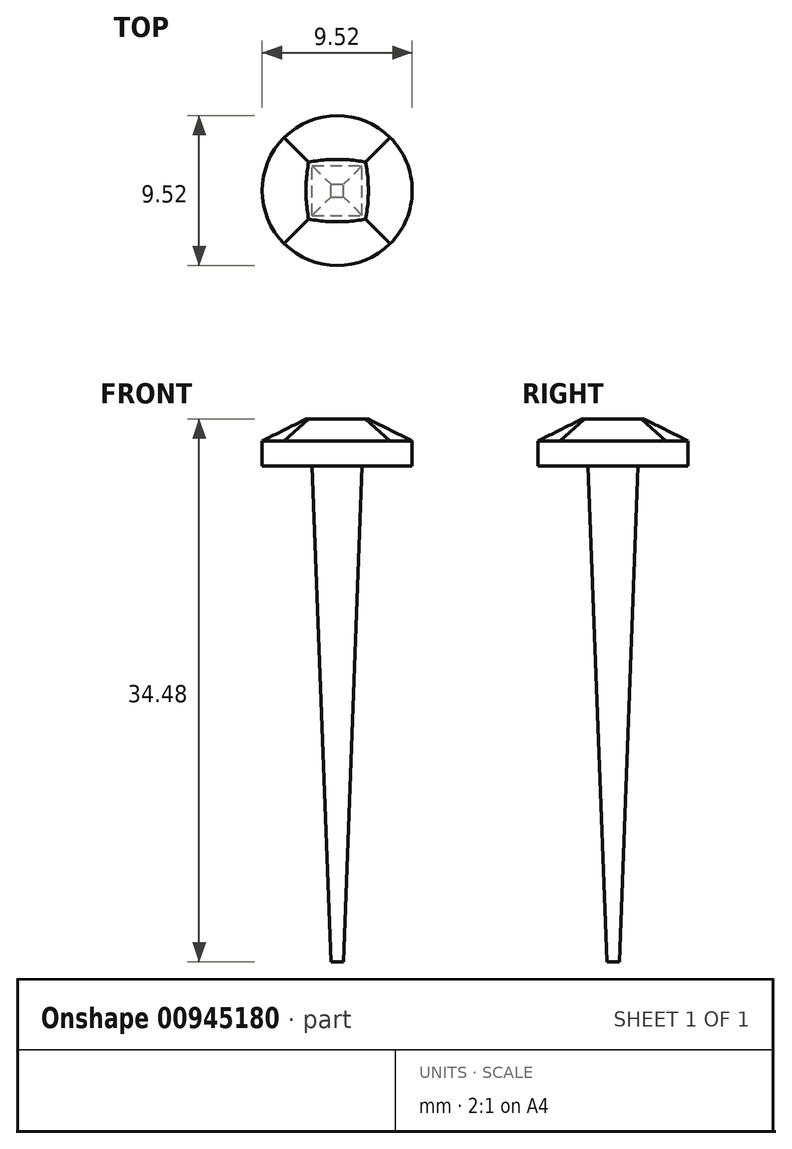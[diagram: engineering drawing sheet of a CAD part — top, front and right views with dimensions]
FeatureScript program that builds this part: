
annotation { "Feature Type Name" : "Feature", "Feature Type Description" : "" }
export const myFeature = defineFeature(function(context is Context, id is Id, definition is map)
    precondition{}
    {
        {
            var Q0;
            Q0=qCreatedBy(makeId("Top.planeOp"),FACE);
            var sketch = newSketch(context, id + "F0", { "sketchPlane" : qUnion([Q0])});
            skCircle(sketch, "E0", {"center": v(0, 0) * mm, "radius": 4.76 * mm});
            skSolve(sketch);
        }
        {
            var Q0;
            Q0=qCreatedBy(makeId("Top.planeOp"),FACE);
            cPlane(context, id + "F1", {"entities" : qUnion([Q0]), "cplaneType" : CPlaneType.OFFSET, "offset" : 1.59 * mm, "width" : 152.4 * mm, "height" : 152.4 * mm});
        }
        {
            var Q0;
            Q0=qCreatedBy(id+"F1.planeOp",FACE);
            var sketch = newSketch(context, id + "F2", { "sketchPlane" : qUnion([Q0])});
            skCircle(sketch, "E1", {"center": v(0, 0) * mm, "radius": 4.76 * mm});
            skSolve(sketch);
        }
        {
            var Q0;
            Q0=qCreatedBy(id+"F1.planeOp",FACE);
            cPlane(context, id + "F3", {"entities" : qUnion([Q0]), "cplaneType" : CPlaneType.OFFSET, "offset" : 1.59 * mm, "width" : 152.4 * mm, "height" : 152.4 * mm});
        }
        {
            var Q0;
            Q0=qCreatedBy(id+"F3.planeOp",FACE);
            var sketch = newSketch(context, id + "F4", { "sketchPlane" : qUnion([Q0])});
            skLineSegment(sketch, "E2.bottom", {"start": v(-1.59, 1.59) * mm, "end": v(1.59, 1.59) * mm});
            skLineSegment(sketch, "E2.top", {"start": v(-1.59, -1.59) * mm, "end": v(1.59, -1.59) * mm});
            skLineSegment(sketch, "E2.left", {"start": v(-1.59, 1.59) * mm, "end": v(-1.59, -1.59) * mm});
            skLineSegment(sketch, "E2.right", {"start": v(1.59, 1.59) * mm, "end": v(1.59, -1.59) * mm});
            skSolve(sketch);
        }
        {
            var Q0;
            Q0=makeQuery(id+"F0.imprint","IMPRINT",FACE,{"disambiguationData":[TD([[makeQuery(id+"F0.imprint","IMPRINT",EDGE,{"derivedFrom":sQuery(id+"F0.wireOp",EDGE,"E0")}),1.0]])]});
            var Q1;
            Q1=makeQuery(id+"F2.imprint","IMPRINT",FACE,{"disambiguationData":[TD([[makeQuery(id+"F2.imprint","IMPRINT",EDGE,{"derivedFrom":sQuery(id+"F2.wireOp",EDGE,"E1")}),1.0]])]});
            loft(context, id + "F5", {"sheetProfilesArray" : [{ "sheetProfileEntities" : qUnion([Q0]) }, { "sheetProfileEntities" : qUnion([Q1]) }]});
        }
        {
            var Q0;
            Q0=makeQuery(id+"F5.opLoft","CAP_FACE",FACE,{"disambiguationData":[OSD([makeQuery(id+"F2.imprint","IMPRINT",FACE,{"disambiguationData":[TD([[makeQuery(id+"F2.imprint","IMPRINT",EDGE,{"derivedFrom":sQuery(id+"F2.wireOp",EDGE,"E1")}),1.0]])]})])],"isStart":true});
            var Q1;
            Q1=makeQuery(id+"F4.imprint","IMPRINT",FACE,{"disambiguationData":[TD([[makeQuery(id+"F4.imprint","IMPRINT",EDGE,{"derivedFrom":sQuery(id+"F4.wireOp",EDGE,"E2.bottom")}),-1.0]])]});
            loft(context, id + "F6", {"operationType" : NewBodyOperationType.ADD, "sheetProfilesArray" : [{ "sheetProfileEntities" : qUnion([Q0]) }, { "sheetProfileEntities" : qUnion([Q1]) }]});
        }
        {
            var Q0;
            Q0=qCreatedBy(makeId("Top.planeOp"),FACE);
            cPlane(context, id + "F7", {"entities" : qUnion([Q0]), "cplaneType" : CPlaneType.OFFSET, "offset" : 31.5 * mm, "oppositeDirection" : true, "width" : 152.4 * mm, "height" : 152.4 * mm});
        }
        {
            var Q0;
            Q0=qCreatedBy(id+"F7.planeOp",FACE);
            var sketch = newSketch(context, id + "F8", { "sketchPlane" : qUnion([Q0])});
            skLineSegment(sketch, "E3.bottom", {"start": v(-0.4, -0.4) * mm, "end": v(0.4, -0.4) * mm});
            skLineSegment(sketch, "E3.top", {"start": v(-0.4, 0.4) * mm, "end": v(0.4, 0.4) * mm});
            skLineSegment(sketch, "E3.left", {"start": v(-0.4, -0.4) * mm, "end": v(-0.4, 0.4) * mm});
            skLineSegment(sketch, "E3.right", {"start": v(0.4, -0.4) * mm, "end": v(0.4, 0.4) * mm});
            skSolve(sketch);
        }
        {
            var Q0;
            Q0=makeQuery(id+"F5.opLoft","CAP_FACE",FACE,{"disambiguationData":[OSD([makeQuery(id+"F0.imprint","IMPRINT",FACE,{"disambiguationData":[TD([[makeQuery(id+"F0.imprint","IMPRINT",EDGE,{"derivedFrom":sQuery(id+"F0.wireOp",EDGE,"E0")}),1.0]])]})])],"isStart":true});
            var sketch = newSketch(context, id + "F9", { "sketchPlane" : qUnion([Q0])});
            skLineSegment(sketch, "E4.bottom", {"start": v(-1.59, 1.59) * mm, "end": v(1.59, 1.59) * mm});
            skLineSegment(sketch, "E4.top", {"start": v(-1.59, -1.59) * mm, "end": v(1.59, -1.59) * mm});
            skLineSegment(sketch, "E4.left", {"start": v(-1.59, 1.59) * mm, "end": v(-1.59, -1.59) * mm});
            skLineSegment(sketch, "E4.right", {"start": v(1.59, 1.59) * mm, "end": v(1.59, -1.59) * mm});
            skSolve(sketch);
        }
        {
            var Q1;
            Q1=makeQuery(id+"F9.imprint","IMPRINT",FACE,{"disambiguationData":[TD([[makeQuery(id+"F9.imprint","IMPRINT",EDGE,{"derivedFrom":sQuery(id+"F9.wireOp",EDGE,"E4.bottom")}),-1.0]])]});
            var Q2;
            Q2=makeQuery(id+"F8.imprint","IMPRINT",FACE,{"disambiguationData":[TD([[makeQuery(id+"F8.imprint","IMPRINT",EDGE,{"derivedFrom":sQuery(id+"F8.wireOp",EDGE,"E3.bottom")}),1.0]])]});
            loft(context, id + "F10", {"operationType" : NewBodyOperationType.ADD, "sheetProfilesArray" : [{ "sheetProfileEntities" : qUnion([Q1]) }, { "sheetProfileEntities" : qUnion([Q2]) }]});
        }
        {
            var Q0;
            Q0=qCreatedBy(id+"F3.planeOp",FACE);
            var sketch = newSketch(context, id + "F11", { "sketchPlane" : qUnion([Q0])});
            skCircle(sketch, "E5", {"center": v(0, 0) * mm, "radius": 2.64 * mm});
            skSolve(sketch);
        }
        {
            var Q0;
            Q0=makeQuery(id+"F11.imprint","IMPRINT",FACE,{"disambiguationData":[TD([[makeQuery(id+"F11.imprint","IMPRINT",EDGE,{"derivedFrom":sQuery(id+"F11.wireOp",EDGE,"E5")}),1.0]])]});
            extrude(context, id + "F12", {"entities" : qUnion([Q0]), "operationType" : NewBodyOperationType.REMOVE, "oppositeDirection" : true, "depth" : 0.2 * mm, "offsetDistance" : 25.4 * mm});
        }
    });
